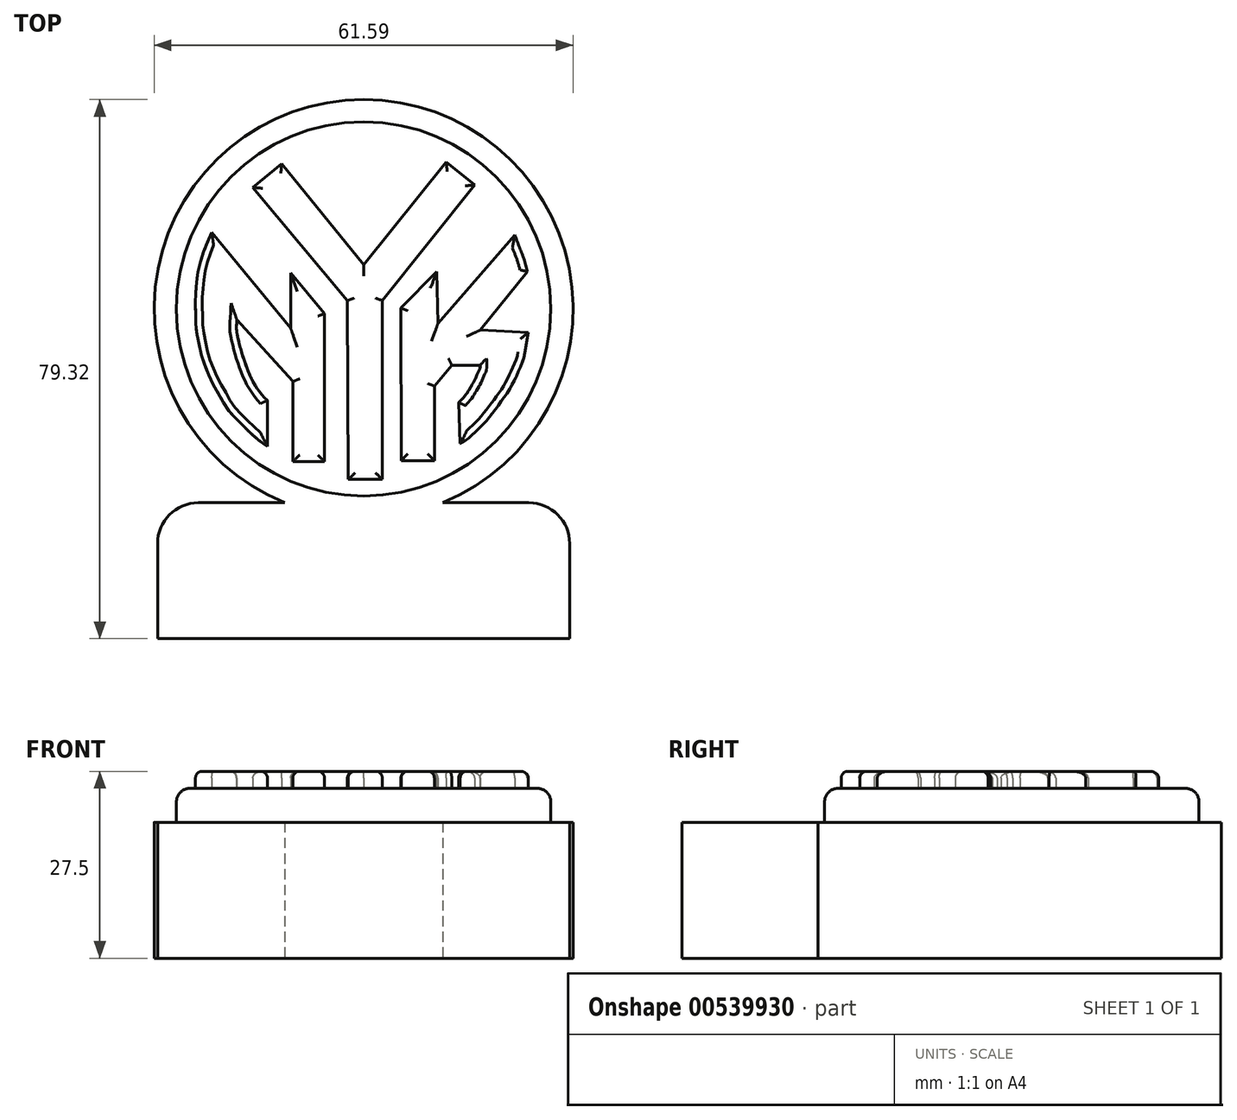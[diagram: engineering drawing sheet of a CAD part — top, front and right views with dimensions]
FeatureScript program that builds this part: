
annotation { "Feature Type Name" : "Feature", "Feature Type Description" : "" }
export const myFeature = defineFeature(function(context is Context, id is Id, definition is map)
    precondition{}
    {
        {
            var Q0;
            Q0=qCreatedBy(makeId("Top.planeOp"),FACE);
            var sketch = newSketch(context, id + "F0", { "sketchPlane" : qUnion([Q0])});
            skLineSegment(sketch, "E0", {"start": v(31.03, 36.84) * mm, "end": v(31.03, 61.33) * mm, "construction": true});
            skLineSegment(sketch, "E1", {"start": v(31.03, 36.84) * mm, "end": v(31.03, 0) * mm, "construction": true});
            skLineSegment(sketch, "E2", {"start": v(0, 30.67) * mm, "end": v(61.33, 30.67) * mm, "construction": true});
            skCircle(sketch, "E3", {"center": v(31.03, 30.67) * mm, "radius": 30.8 * mm});
            skLineSegment(sketch, "E4.bottom", {"start": v(61.33, 2.14) * mm, "end": v(0.72, 2.14) * mm});
            skLineSegment(sketch, "E4.top", {"start": v(61.33, -17.86) * mm, "end": v(0.72, -17.86) * mm});
            skLineSegment(sketch, "E4.left", {"start": v(61.33, 2.14) * mm, "end": v(61.33, -17.86) * mm});
            skLineSegment(sketch, "E4.right", {"start": v(0.72, 2.14) * mm, "end": v(0.72, -17.86) * mm});
            skPoint(sketch, "E4.middle", {"position": v(31.03, -7.86) * mm});
            skSolve(sketch);
        }
        {
            var Q0;
            Q0 = qSketchRegion(id + "F0", true);
            extrude(context, id + "F1", {"entities" : qUnion([Q0]), "depth" : 20 * mm, "offsetDistance" : 25 * mm});
        }
        {
            var Q0;
            Q0=makeQuery(id+"F1.opExtrude","CAP_FACE",FACE,{"disambiguationData":[OSD([sQuery(id+"F0.wireOp",EDGE,"E3"),sQuery(id+"F0.wireOp",EDGE,"E4.bottom"),sQuery(id+"F0.wireOp",EDGE,"E4.top"),sQuery(id+"F0.wireOp",EDGE,"E4.left"),sQuery(id+"F0.wireOp",EDGE,"E4.right")])],"isStart":false});
            var sketch = newSketch(context, id + "F2", { "sketchPlane" : qUnion([Q0])});
            skCircle(sketch, "E5", {"center": v(31.03, 30.67) * mm, "radius": 27.53 * mm});
            skSolve(sketch);
        }
        {
            var Q0;
            Q0 = qSketchRegion(id + "F2", true);
            extrude(context, id + "F3", {"entities" : qUnion([Q0]), "operationType" : NewBodyOperationType.ADD, "depth" : 5 * mm, "offsetDistance" : 25 * mm});
        }
        {
            var Q0;
            Q0=makeQuery(id+"F3.opExtrude","CAP_FACE",FACE,{"disambiguationData":[OSD([sQuery(id+"F2.wireOp",EDGE,"E5")])],"isStart":false});
            var sketch = newSketch(context, id + "F4", { "sketchPlane" : qUnion([Q0])});
            skLineSegment(sketch, "E6", {"start": v(28.76, 5.58) * mm, "end": v(33.78, 5.58) * mm});
            skLineSegment(sketch, "E7", {"start": v(33.78, 5.58) * mm, "end": v(33.78, 31.9) * mm});
            skLineSegment(sketch, "E8", {"start": v(33.78, 31.9) * mm, "end": v(47.38, 48.92) * mm});
            skLineSegment(sketch, "E9", {"start": v(47.38, 48.92) * mm, "end": v(43.17, 52.29) * mm});
            skLineSegment(sketch, "E10", {"start": v(43.17, 52.29) * mm, "end": v(31.05, 37.13) * mm});
            skLineSegment(sketch, "E11", {"start": v(31.05, 37.13) * mm, "end": v(19, 52) * mm});
            skLineSegment(sketch, "E12", {"start": v(19, 52) * mm, "end": v(14.74, 48.55) * mm});
            skLineSegment(sketch, "E13", {"start": v(14.74, 48.55) * mm, "end": v(28.65, 31.9) * mm});
            skLineSegment(sketch, "E14", {"start": v(28.65, 31.9) * mm, "end": v(28.76, 5.58) * mm});
            skLineSegment(sketch, "E15", {"start": v(8.71, 41.91) * mm, "end": v(20.3, 27.8) * mm});
            skLineSegment(sketch, "E16", {"start": v(20.3, 27.8) * mm, "end": v(20.3, 35.98) * mm});
            skLineSegment(sketch, "E17", {"start": v(20.3, 35.98) * mm, "end": v(25.28, 29.97) * mm});
            skLineSegment(sketch, "E18", {"start": v(25.28, 29.97) * mm, "end": v(25.28, 8.17) * mm});
            skLineSegment(sketch, "E19", {"start": v(25.28, 8.17) * mm, "end": v(20.62, 8.17) * mm});
            skLineSegment(sketch, "E20", {"start": v(20.62, 8.17) * mm, "end": v(20.62, 19.99) * mm});
            skLineSegment(sketch, "E21", {"start": v(20.62, 19.99) * mm, "end": v(12.39, 29.07) * mm});
            skFitSpline(sketch, "E22", {"points": [v(12.39, 29.07) * mm, v(12.35, 27.59) * mm, v(12.56, 26.37) * mm, v(13.12, 24.18) * mm, v(13.88, 21.93) * mm, v(14.76, 19.95) * mm, v(15.77, 18.4) * mm, v(16.57, 17.46) * mm, v(16.88, 17.25) * mm], "startDerivative": vector(-0.86, -12.67) * mm, "endDerivative": vector(4.63, -2.66) * mm});
            skLineSegment(sketch, "E23", {"start": v(16.88, 17.25) * mm, "end": v(16.88, 10.45) * mm});
            skFitSpline(sketch, "E24", {"points": [v(16.88, 10.45) * mm, v(15.8, 11.2) * mm, v(14.9, 11.96) * mm, v(14.04, 12.75) * mm, v(13.06, 13.75) * mm, v(12.34, 14.46) * mm, v(11.4, 15.46) * mm, v(10.6, 16.57) * mm, v(10.01, 17.66) * mm, v(9.35, 18.83) * mm, v(8.72, 19.9) * mm, v(8.39, 20.65) * mm, v(7.86, 21.87) * mm, v(7.35, 23.26) * mm, v(7.13, 24.14) * mm, v(6.81, 25.45) * mm, v(6.68, 26.13) * mm, v(6.42, 27.63) * mm, v(6.35, 29.2) * mm, v(6.3, 31.05) * mm, v(6.37, 33.28) * mm, v(6.5, 34.89) * mm, v(6.7, 36.12) * mm, v(7.27, 38.36) * mm, v(8.12, 40.6) * mm, v(8.71, 41.91) * mm], "startDerivative": vector(-28.43, 18.59) * mm, "endDerivative": vector(13.99, 30.2) * mm});
            skLineSegment(sketch, "E25", {"start": v(36.5, 30.8) * mm, "end": v(41.8, 36.12) * mm});
            skLineSegment(sketch, "E26", {"start": v(41.8, 36.12) * mm, "end": v(41.97, 28.55) * mm});
            skLineSegment(sketch, "E27", {"start": v(41.97, 28.55) * mm, "end": v(53.26, 41.55) * mm});
            skFitSpline(sketch, "E28", {"points": [v(53.26, 41.55) * mm, v(53.9, 39.83) * mm, v(54.65, 37.9) * mm, v(55.08, 36.16) * mm], "startDerivative": vector(1.86, -5.16) * mm, "endDerivative": vector(1.12, -5.29) * mm});
            skLineSegment(sketch, "E29", {"start": v(55.08, 36.16) * mm, "end": v(48.18, 27.54) * mm});
            skLineSegment(sketch, "E30", {"start": v(48.18, 27.54) * mm, "end": v(55.26, 27.18) * mm});
            skLineSegment(sketch, "E31", {"start": v(55.26, 27.18) * mm, "end": v(54.71, 24.19) * mm});
            skFitSpline(sketch, "E32", {"points": [v(54.71, 24.19) * mm, v(54.43, 22.97) * mm, v(53.95, 21.87) * mm, v(53.57, 20.93) * mm, v(53.04, 19.9) * mm, v(52.46, 18.78) * mm, v(51.82, 17.87) * mm, v(51.17, 16.93) * mm, v(50.22, 15.66) * mm, v(49.42, 14.66) * mm, v(48.73, 13.82) * mm, v(48, 13.07) * mm, v(47, 12.14) * mm, v(46.08, 11.36) * mm, v(45.24, 10.86) * mm], "startDerivative": vector(-2.94, -16.9) * mm, "endDerivative": vector(-13.1, -6.97) * mm});
            skLineSegment(sketch, "E33", {"start": v(45.24, 10.86) * mm, "end": v(44.99, 16.88) * mm});
            skFitSpline(sketch, "E34", {"points": [v(44.99, 16.88) * mm, v(45.42, 17.3) * mm, v(46.15, 18.16) * mm, v(46.7, 19.05) * mm, v(47.15, 19.81) * mm, v(47.65, 20.82) * mm, v(47.96, 21.5) * mm, v(48.14, 21.95) * mm, v(48.15, 22.4) * mm], "startDerivative": vector(3.7, 3.4) * mm, "endDerivative": vector(-0.24, 4.76) * mm});
            skLineSegment(sketch, "E35", {"start": v(48.15, 22.4) * mm, "end": v(43.99, 22.4) * mm});
            skLineSegment(sketch, "E36", {"start": v(43.99, 22.4) * mm, "end": v(41.43, 19.33) * mm});
            skLineSegment(sketch, "E37", {"start": v(41.43, 19.33) * mm, "end": v(41.43, 8.33) * mm});
            skLineSegment(sketch, "E38", {"start": v(41.43, 8.33) * mm, "end": v(36.55, 8.33) * mm});
            skLineSegment(sketch, "E39", {"start": v(36.55, 8.33) * mm, "end": v(36.5, 30.8) * mm});
            skSolve(sketch);
        }
        {
            var Q0;
            Q0 = qSketchRegion(id + "F4", true);
            extrude(context, id + "F5", {"entities" : qUnion([Q0]), "operationType" : NewBodyOperationType.ADD, "depth" : 2.5 * mm, "offsetDistance" : 25 * mm});
        }
        {
            var Q0;
            Q0=makeQuery(id+"F3.opExtrude","CAP_EDGE",EDGE,{"disambiguationData":[OSD([sQuery(id+"F2.wireOp",EDGE,"E5")])],"isStart":false});
            fillet(context, id + "F6", {"entities" : qUnion([Q0]), "radius" : 2 * mm, "tangentPropagation" : true, "allowEdgeOverflow" : false});
        }
        {
            var Q0;
            Q0=makeQuery(id+"F5.opExtrude","CAP_FACE",FACE,{"disambiguationData":[OSD([sQuery(id+"F4.wireOp",EDGE,"E15"),sQuery(id+"F4.wireOp",EDGE,"E16"),sQuery(id+"F4.wireOp",EDGE,"E17"),sQuery(id+"F4.wireOp",EDGE,"E18"),sQuery(id+"F4.wireOp",EDGE,"E19"),sQuery(id+"F4.wireOp",EDGE,"E20"),sQuery(id+"F4.wireOp",EDGE,"E21"),sQuery(id+"F4.wireOp",EDGE,"E22"),sQuery(id+"F4.wireOp",EDGE,"E23"),sQuery(id+"F4.wireOp",EDGE,"E24")])],"isStart":false});
            var Q1;
            Q1=makeQuery(id+"F5.opExtrude","CAP_FACE",FACE,{"disambiguationData":[OSD([sQuery(id+"F4.wireOp",EDGE,"E6"),sQuery(id+"F4.wireOp",EDGE,"E7"),sQuery(id+"F4.wireOp",EDGE,"E8"),sQuery(id+"F4.wireOp",EDGE,"E9"),sQuery(id+"F4.wireOp",EDGE,"E10"),sQuery(id+"F4.wireOp",EDGE,"E11"),sQuery(id+"F4.wireOp",EDGE,"E12"),sQuery(id+"F4.wireOp",EDGE,"E13"),sQuery(id+"F4.wireOp",EDGE,"E14")])],"isStart":false});
            var Q2;
            Q2=makeQuery(id+"F5.opExtrude","CAP_FACE",FACE,{"disambiguationData":[OSD([sQuery(id+"F4.wireOp",EDGE,"E25"),sQuery(id+"F4.wireOp",EDGE,"E26"),sQuery(id+"F4.wireOp",EDGE,"E27"),sQuery(id+"F4.wireOp",EDGE,"E28"),sQuery(id+"F4.wireOp",EDGE,"E29"),sQuery(id+"F4.wireOp",EDGE,"E30"),sQuery(id+"F4.wireOp",EDGE,"E31"),sQuery(id+"F4.wireOp",EDGE,"E32"),sQuery(id+"F4.wireOp",EDGE,"E33"),sQuery(id+"F4.wireOp",EDGE,"E34"),sQuery(id+"F4.wireOp",EDGE,"E35"),sQuery(id+"F4.wireOp",EDGE,"E36"),sQuery(id+"F4.wireOp",EDGE,"E37"),sQuery(id+"F4.wireOp",EDGE,"E38"),sQuery(id+"F4.wireOp",EDGE,"E39")])],"isStart":false});
            fillet(context, id + "F7", {"entities" : qUnion([Q0, Q1, Q2]), "radius" : 1 * mm, "tangentPropagation" : true, "allowEdgeOverflow" : false});
        }
        {
            var Q0;
            Q0=makeQuery(id+"F1.opExtrude","SWEPT_EDGE",EDGE,{"disambiguationData":[OSD([sQuery(id+"F0.wireOp",EDGE,"E4.bottom"),sQuery(id+"F0.wireOp",EDGE,"E4.right")])]});
            var Q1;
            Q1=makeQuery(id+"F1.opExtrude","SWEPT_EDGE",EDGE,{"disambiguationData":[OSD([sQuery(id+"F0.wireOp",EDGE,"E4.bottom"),sQuery(id+"F0.wireOp",EDGE,"E4.left")])]});
            fillet(context, id + "F8", {"entities" : qUnion([Q0, Q1]), "radius" : 6 * mm, "tangentPropagation" : true, "allowEdgeOverflow" : false});
        }
    });
